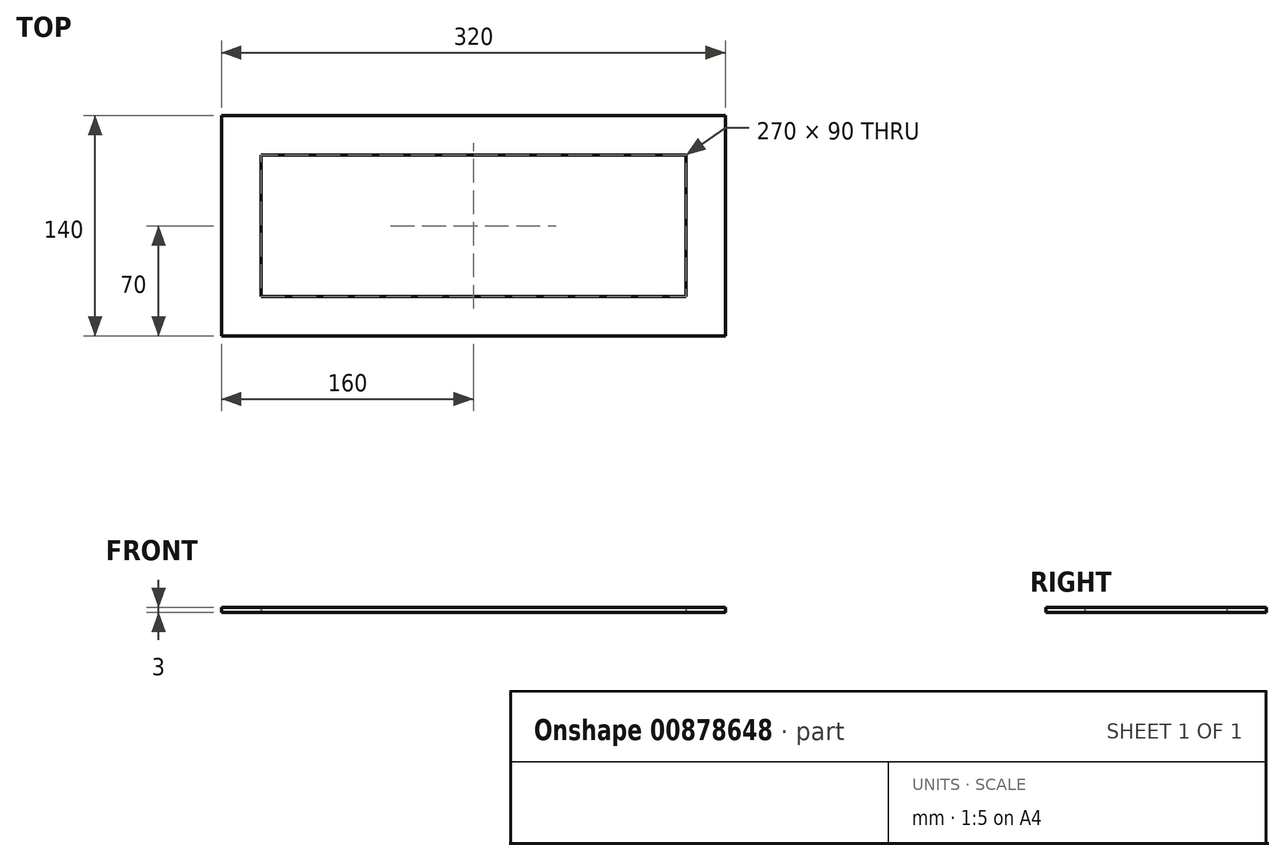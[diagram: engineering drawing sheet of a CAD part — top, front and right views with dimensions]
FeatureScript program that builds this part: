
annotation { "Feature Type Name" : "Feature", "Feature Type Description" : "" }
export const myFeature = defineFeature(function(context is Context, id is Id, definition is map)
    precondition{}
    {
        {
            var Q0;
            Q0=qCreatedBy(makeId("Top.planeOp"),FACE);
            var sketch = newSketch(context, id + "F0", { "sketchPlane" : qUnion([Q0])});
            skLineSegment(sketch, "E0.bottom", {"start": v(160, -70) * mm, "end": v(-160, -70) * mm});
            skLineSegment(sketch, "E0.top", {"start": v(160, 70) * mm, "end": v(-160, 70) * mm});
            skLineSegment(sketch, "E0.left", {"start": v(160, -70) * mm, "end": v(160, 70) * mm});
            skLineSegment(sketch, "E0.right", {"start": v(-160, -70) * mm, "end": v(-160, 70) * mm});
            skPoint(sketch, "E0.middle", {"position": v(0, 0) * mm});
            skLineSegment(sketch, "E1.bottom", {"start": v(135, -45) * mm, "end": v(-135, -45) * mm});
            skLineSegment(sketch, "E1.top", {"start": v(135, 45) * mm, "end": v(-135, 45) * mm});
            skLineSegment(sketch, "E1.left", {"start": v(135, -45) * mm, "end": v(135, 45) * mm});
            skLineSegment(sketch, "E1.right", {"start": v(-135, -45) * mm, "end": v(-135, 45) * mm});
            skSolve(sketch);
        }
        {
            var Q0;
            Q0=makeQuery(id+"F0.imprint","IMPRINT",FACE,{"disambiguationData":[TD([[makeQuery(id+"F0.imprint","IMPRINT",EDGE,{"derivedFrom":sQuery(id+"F0.wireOp",EDGE,"E0.bottom")}),-1.0]])]});
            extrude(context, id + "F1", {"entities" : qUnion([Q0]), "depth" : 3 * mm, "offsetDistance" : 25 * mm});
        }
    });
